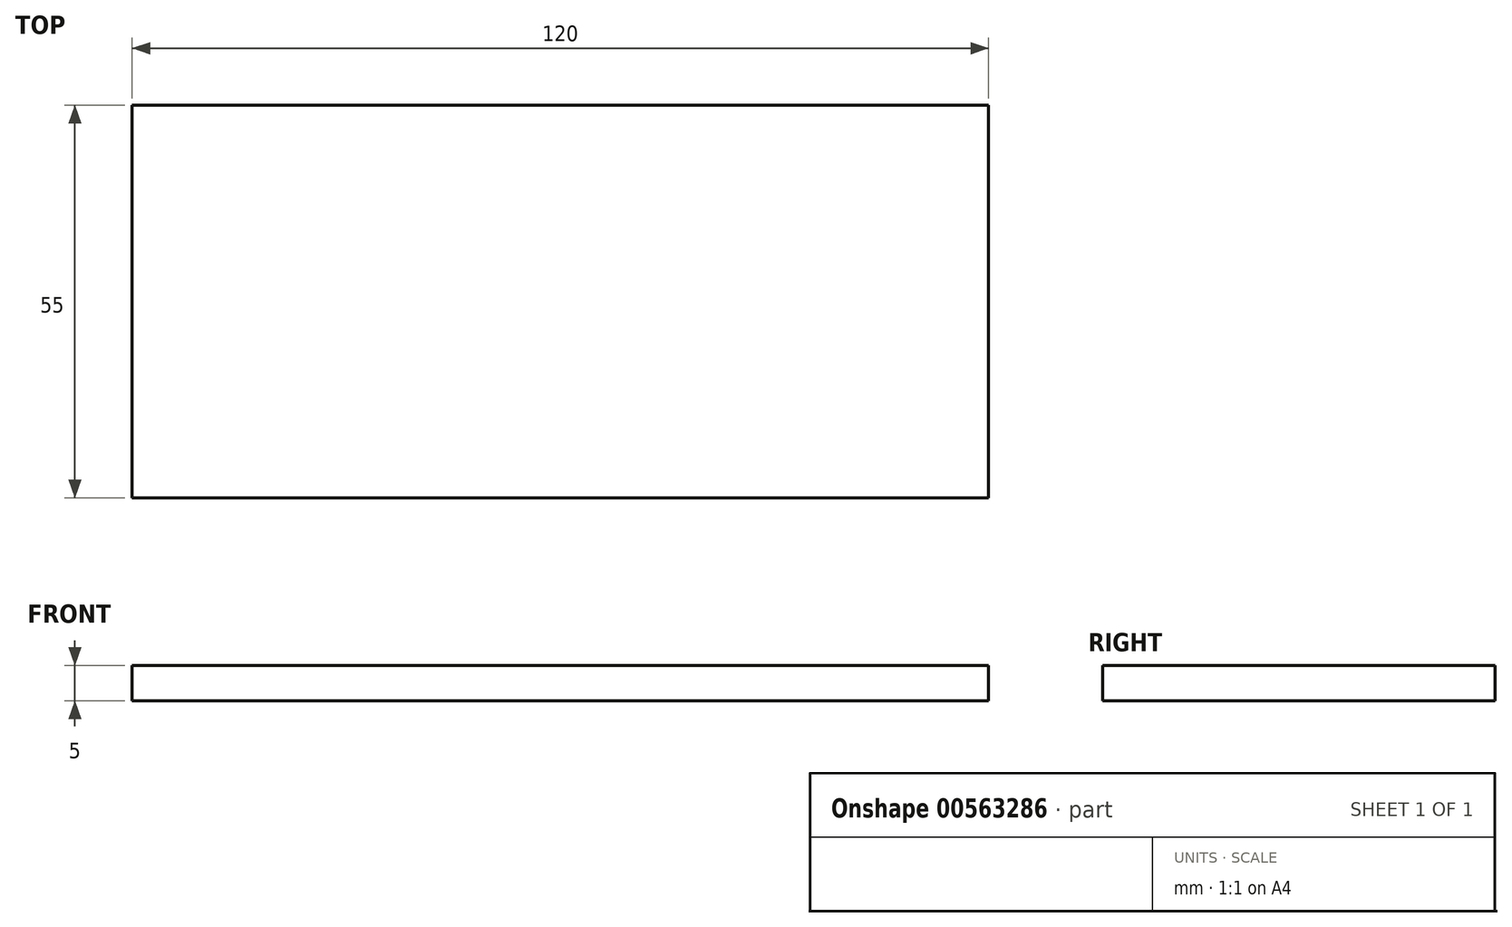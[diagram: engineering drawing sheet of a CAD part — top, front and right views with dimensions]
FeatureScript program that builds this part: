
annotation { "Feature Type Name" : "Feature", "Feature Type Description" : "" }
export const myFeature = defineFeature(function(context is Context, id is Id, definition is map)
    precondition{}
    {
        {
            var Q0;
            Q0=qCreatedBy(makeId("Top.planeOp"),FACE);
            var sketch = newSketch(context, id + "F0", { "sketchPlane" : qUnion([Q0])});
            skLineSegment(sketch, "E0.bottom", {"start": v(60, 27.5) * mm, "end": v(-60, 27.5) * mm});
            skLineSegment(sketch, "E0.top", {"start": v(60, -27.5) * mm, "end": v(-60, -27.5) * mm});
            skLineSegment(sketch, "E0.left", {"start": v(60, 27.5) * mm, "end": v(60, -27.5) * mm});
            skLineSegment(sketch, "E0.right", {"start": v(-60, 27.5) * mm, "end": v(-60, -27.5) * mm});
            skPoint(sketch, "E0.middle", {"position": v(0, 0) * mm});
            skSolve(sketch);
        }
        {
            var Q0;
            Q0 = qSketchRegion(id + "F0", true);
            extrude(context, id + "F1", {"entities" : qUnion([Q0]), "depth" : 5 * mm, "offsetDistance" : 25 * mm});
        }
    });
